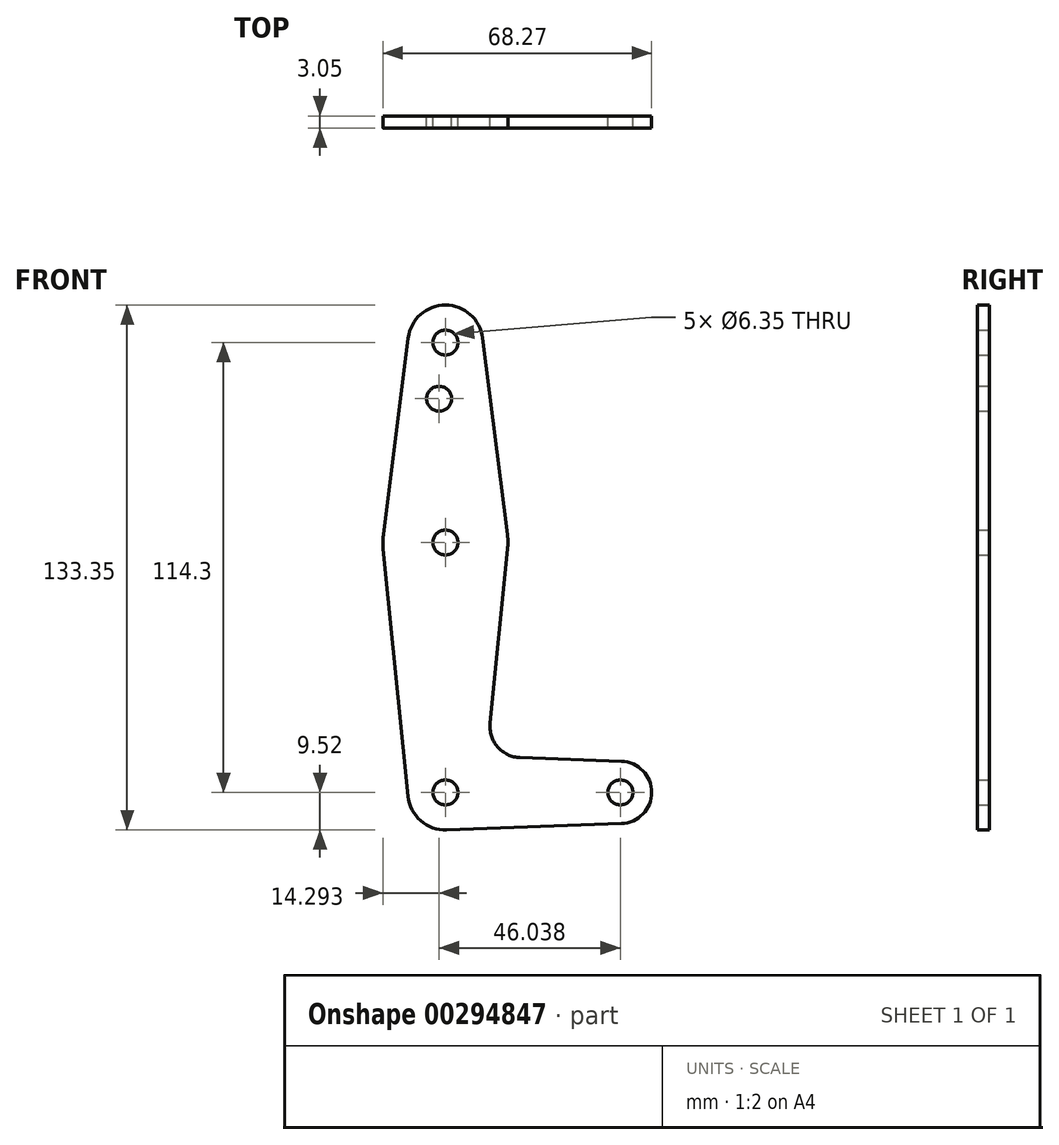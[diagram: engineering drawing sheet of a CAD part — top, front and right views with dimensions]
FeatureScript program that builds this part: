
annotation { "Feature Type Name" : "Feature", "Feature Type Description" : "" }
export const myFeature = defineFeature(function(context is Context, id is Id, definition is map)
    precondition{}
    {
        {
            var Q0;
            Q0=qCreatedBy(makeId("Front.planeOp"),FACE);
            var sketch = newSketch(context, id + "F0", { "sketchPlane" : qUnion([Q0])});
            skCircle(sketch, "E0", {"center": v(0, 0) * mm, "radius": 9.53 * mm});
            skLineSegment(sketch, "E1", {"start": v(0, 0) * mm, "end": v(44.45, 0) * mm, "construction": true});
            skCircle(sketch, "E2", {"center": v(44.45, 0) * mm, "radius": 7.94 * mm});
            skLineSegment(sketch, "E3", {"start": v(0, 0) * mm, "end": v(0, 63.5) * mm, "construction": true});
            skCircle(sketch, "E4", {"center": v(0, 63.5) * mm, "radius": 15.88 * mm});
            skCircle(sketch, "E5", {"center": v(0, 114.3) * mm, "radius": 9.52 * mm});
            skLineSegment(sketch, "E6", {"start": v(0, 114.3) * mm, "end": v(0, 63.5) * mm, "construction": true});
            skLineSegment(sketch, "E7", {"start": v(9.45, 115.5) * mm, "end": v(15.75, 65.48) * mm});
            skLineSegment(sketch, "E8", {"start": v(-15.8, 61.91) * mm, "end": v(-9.48, -0.95) * mm});
            skLineSegment(sketch, "E9", {"start": v(15.8, 61.91) * mm, "end": v(11.34, 17.6) * mm});
            skLineSegment(sketch, "E10", {"start": v(18.97, 8.85) * mm, "end": v(44.73, 7.93) * mm});
            skLineSegment(sketch, "E11", {"start": v(-9.45, 115.5) * mm, "end": v(-15.75, 65.48) * mm});
            skCircle(sketch, "E12", {"center": v(0, 114.3) * mm, "radius": 3.18 * mm});
            skCircle(sketch, "E13", {"center": v(-1.59, 100.03) * mm, "radius": 3.18 * mm});
            skCircle(sketch, "E14", {"center": v(0, 63.5) * mm, "radius": 3.18 * mm});
            skCircle(sketch, "E15", {"center": v(0, 0) * mm, "radius": 3.18 * mm});
            skCircle(sketch, "E16", {"center": v(44.45, 0) * mm, "radius": 3.18 * mm});
            skArc(sketch, "E17.filletArc", {"start": v(11.34, 17.6) * mm, "mid": v(13.26, 11.57) * mm, "end": v(18.97, 8.85) * mm});
            skLineSegment(sketch, "E18", {"start": v(0.34, -9.52) * mm, "end": v(44.73, -7.93) * mm});
            skSolve(sketch);
        }
        {
            var Q0;
            Q0 = qSketchRegion(id + "F0", true);
            extrude(context, id + "F1", {"entities" : qUnion([Q0]), "depth" : 3.05 * mm});
        }
    });
